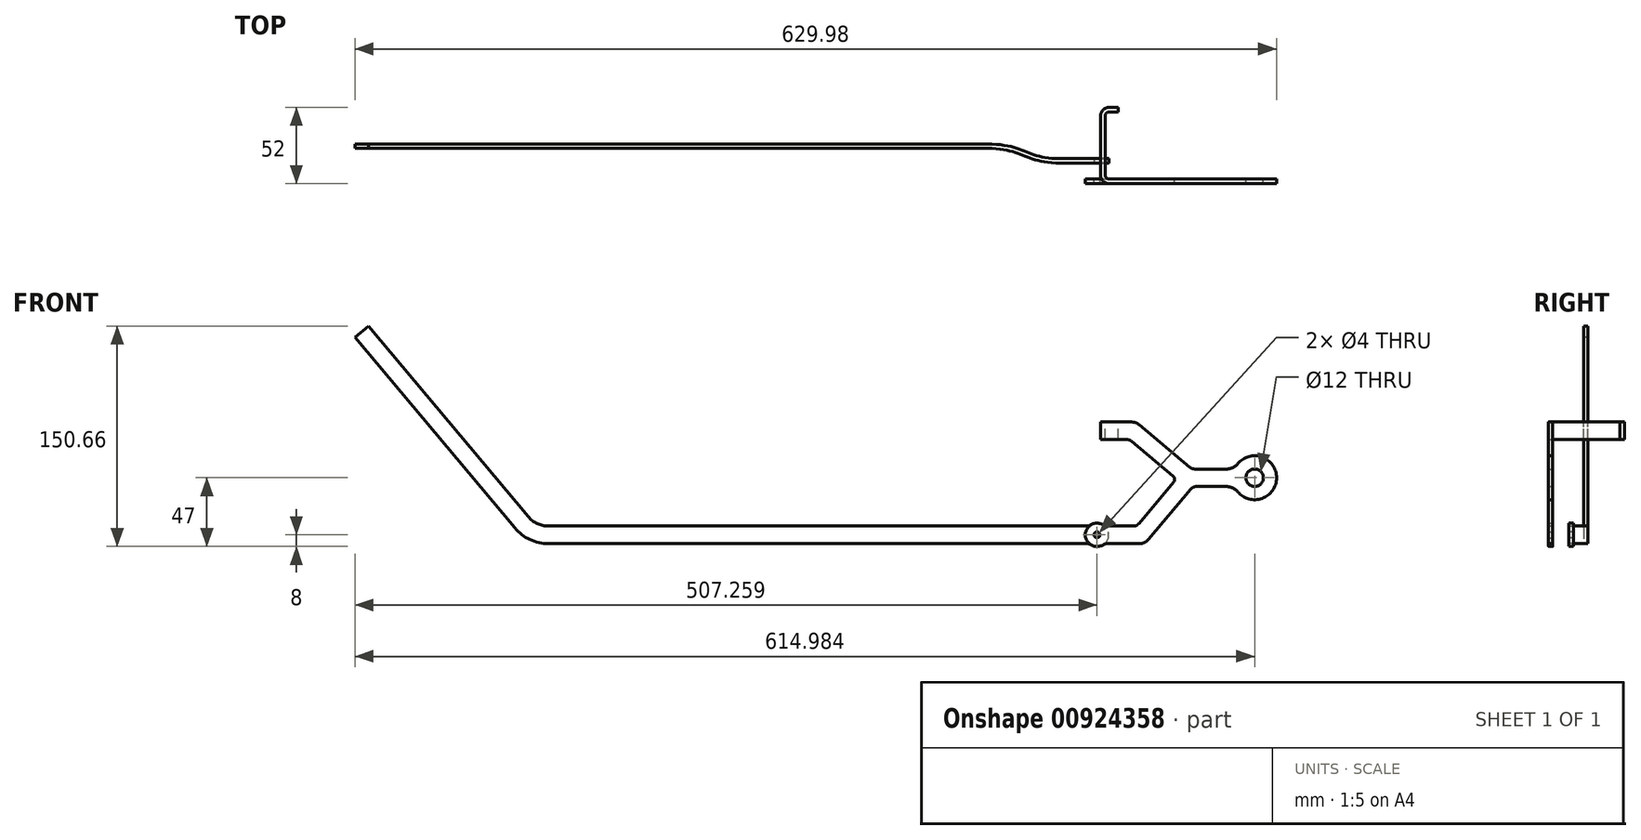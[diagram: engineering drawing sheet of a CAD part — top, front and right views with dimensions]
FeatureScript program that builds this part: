
annotation { "Feature Type Name" : "Feature", "Feature Type Description" : "" }
export const myFeature = defineFeature(function(context is Context, id is Id, definition is map)
    precondition{}
    {
        {
            var Q0;
            Q0=qCreatedBy(makeId("Front.planeOp"),FACE);
            var sketch = newSketch(context, id + "F0", { "sketchPlane" : qUnion([Q0])});
            skLineSegment(sketch, "E0", {"start": v(13.99, 0) * mm, "end": v(313.99, 0) * mm});
            skLineSegment(sketch, "E1", {"start": v(-9, 10.72) * mm, "end": v(-118.27, 140.94) * mm});
            skLineSegment(sketch, "E2", {"start": v(-23.81, 6) * mm, "end": v(-4.01, 6) * mm, "construction": true});
            skPoint(sketch, "E3.visualSharp", {"position": v(0, 0) * mm});
            skArc(sketch, "E3.filletArc", {"start": v(-9, 10.72) * mm, "mid": v(1.31, 2.81) * mm, "end": v(13.99, 0) * mm});
            skLineSegment(sketch, "E4.0", {"start": v(13.99, 12) * mm, "end": v(313.99, 12) * mm});
            skArc(sketch, "E4.1", {"start": v(0.2, 18.43) * mm, "mid": v(6.38, 13.69) * mm, "end": v(13.99, 12) * mm});
            skLineSegment(sketch, "E4.2", {"start": v(0.2, 18.43) * mm, "end": v(-109.07, 148.66) * mm});
            skLineSegment(sketch, "E5", {"start": v(-109.07, 148.66) * mm, "end": v(-118.27, 140.94) * mm});
            skLineSegment(sketch, "E6", {"start": v(313.99, 12) * mm, "end": v(313.99, 0) * mm});
            skSolve(sketch);
        }
        {
            var Q0;
            Q0=makeQuery(id+"F0.imprint","IMPRINT",FACE,{"disambiguationData":[TD([[makeQuery(id+"F0.imprint","IMPRINT",EDGE,{"derivedFrom":sQuery(id+"F0.wireOp",EDGE,"E0")}),1.0]])]});
            extrude(context, id + "F1", {"entities" : qUnion([Q0]), "depth" : 3 * mm, "offsetDistance" : 25 * mm});
        }
        {
            var Q0;
            Q0=qCreatedBy(makeId("Top.planeOp"),FACE);
            var sketch = newSketch(context, id + "F2", { "sketchPlane" : qUnion([Q0])});
            skLineSegment(sketch, "E7.0", {"start": v(13.99, 0) * mm, "end": v(313.99, 0) * mm});
            skSolve(sketch);
        }
        {
            var Q0;
            Q0=makeQuery(id+"F1.opExtrude","CAP_FACE",FACE,{"disambiguationData":[OSD([sQuery(id+"F0.wireOp",EDGE,"E0"),sQuery(id+"F0.wireOp",EDGE,"E1"),sQuery(id+"F0.wireOp",EDGE,"E3.filletArc"),sQuery(id+"F0.wireOp",EDGE,"E4.0"),sQuery(id+"F0.wireOp",EDGE,"E4.1"),sQuery(id+"F0.wireOp",EDGE,"E4.2"),sQuery(id+"F0.wireOp",EDGE,"E5"),sQuery(id+"F0.wireOp",EDGE,"E6")])],"isStart":true});
            cPlane(context, id + "F3", {"entities" : qUnion([Q0]), "cplaneType" : CPlaneType.OFFSET, "offset" : 25 * mm, "width" : 150 * mm, "height" : 150 * mm});
        }
        {
            var Q0;
            Q0=makeQuery(id+"F1.opExtrude","SWEPT_FACE",FACE,{"disambiguationData":[OSD([sQuery(id+"F0.wireOp",EDGE,"E0")])]});
            var sketch = newSketch(context, id + "F4", { "sketchPlane" : qUnion([Q0])});
            skPoint(sketch, "E8.0", {"position": v(313.99, 0) * mm});
            skFitSpline(sketch, "E9", {"points": [v(313.99, 0) * mm, v(363.99, -10) * mm], "startDerivative": vector(75, 0) * mm, "endDerivative": vector(75, 0) * mm});
            skLineSegment(sketch, "E10", {"start": v(363.99, -10) * mm, "end": v(388.99, -10) * mm});
            skLineSegment(sketch, "E11", {"start": v(363.99, -10) * mm, "end": v(241.15, -10) * mm, "construction": true});
            skSolve(sketch);
        }
        {
            var Q0;
            Q0=makeQuery(id+"F1.opExtrude","SWEPT_FACE",FACE,{"disambiguationData":[OSD([sQuery(id+"F0.wireOp",EDGE,"E6")])]});
            var Q1;
            Q1=sQuery(id+"F4.wireOp",EDGE,"E9");
            var Q2;
            Q2=sQuery(id+"F4.wireOp",EDGE,"E10");
            sweep(context, id + "F5", {"operationType" : NewBodyOperationType.ADD, "profiles" : qUnion([Q0]), "path" : qUnion([Q1, Q2])});
        }
        {
            var Q0;
            {var subQ0=sQuery(id+"F4.wireOp",EDGE,"E10");var subQ1=sQuery(id+"F0.wireOp",EDGE,"E6");Q0=makeQuery(id+"F5.opSweep","SWEPT_FACE",FACE,{"disambiguationData":[OSD([subQ1,subQ0]),TDD([makeQuery(id+"F1.opExtrude","CAP_EDGE",EDGE,{"disambiguationData":[OSD([subQ1])],"isStart":true}),subQ0])]});}
            var sketch = newSketch(context, id + "F6", { "sketchPlane" : qUnion([Q0])});
            skCircle(sketch, "E12", {"center": v(-388.99, 6) * mm, "radius": 6 * mm});
            skCircle(sketch, "E13", {"center": v(-388.99, 6) * mm, "radius": 2 * mm});
            skCircle(sketch, "E14", {"center": v(-388.99, 6) * mm, "radius": 8 * mm});
            skSolve(sketch);
        }
        {
            var Q0;
            {var subQ2=sQuery(id+"F0.wireOp",EDGE,"E6");var subQ4=sQuery(id+"F4.wireOp",EDGE,"E10");var subQ5=sQuery(id+"F0.wireOp",EDGE,"E0");var subQ6=makeQuery(id+"F5.opSweep","SWEPT_EDGE",EDGE,{"disambiguationData":[OSD([subQ5,subQ2,subQ4]),TDD([makeQuery(id+"F1.opExtrude","CAP_VERTEX",VERTEX,{"disambiguationData":[OSD([subQ5,subQ2])],"isStart":true}),subQ4])]});var subQ11=sQuery(id+"F6.wireOp",EDGE,"E14");var subQ13=makeQuery(id+"F6.imprint","INTERSECT",VERTEX,{"derivedFrom":[subQ6,subQ11]});Q0=makeQuery(id+"F6.imprint","IMPRINT",FACE,{"disambiguationData":[TD([[makeQuery(id+"F6.imprint","IMPRINT",EDGE,{"disambiguationData":[TD([[subQ13,1.0]])],"derivedFrom":subQ11}),1.0]])]});}
            var Q1;
            {var subQ1=sQuery(id+"F4.wireOp",VERTEX,"E10.end");var subQ2=sQuery(id+"F0.wireOp",EDGE,"E6");var subQ3=makeQuery(id+"F5.opSweep","CAP_EDGE",EDGE,{"disambiguationData":[OSD([subQ2,subQ1]),TDD([makeQuery(id+"F1.opExtrude","CAP_EDGE",EDGE,{"disambiguationData":[OSD([subQ2])],"isStart":true}),subQ1])],"isStart":false});var subQ9=sQuery(id+"F6.wireOp",EDGE,"E13");var subQ10=makeQuery(id+"F6.imprint","INTERSECT",VERTEX,{"disambiguationData":[OD(0.0)],"derivedFrom":[subQ3,subQ9]});Q1=makeQuery(id+"F6.imprint","IMPRINT",FACE,{"disambiguationData":[TD([[makeQuery(id+"F6.imprint","IMPRINT",EDGE,{"disambiguationData":[TD([[subQ10,1.0]])],"derivedFrom":subQ9}),-1.0]])]});}
            var Q2;
            {var subQ1=sQuery(id+"F4.wireOp",VERTEX,"E10.end");var subQ2=sQuery(id+"F0.wireOp",EDGE,"E6");var subQ3=makeQuery(id+"F5.opSweep","CAP_EDGE",EDGE,{"disambiguationData":[OSD([subQ2,subQ1]),TDD([makeQuery(id+"F1.opExtrude","CAP_EDGE",EDGE,{"disambiguationData":[OSD([subQ2])],"isStart":true}),subQ1])],"isStart":false});var subQ9=sQuery(id+"F6.wireOp",EDGE,"E13");var subQ10=makeQuery(id+"F6.imprint","INTERSECT",VERTEX,{"disambiguationData":[OD(0.0)],"derivedFrom":[subQ3,subQ9]});Q2=makeQuery(id+"F6.imprint","IMPRINT",FACE,{"disambiguationData":[TD([[makeQuery(id+"F6.imprint","IMPRINT",EDGE,{"disambiguationData":[TD([[subQ10,-1.0]])],"derivedFrom":subQ9}),-1.0]])]});}
            var Q3;
            {var subQ2=sQuery(id+"F0.wireOp",EDGE,"E6");var subQ4=sQuery(id+"F4.wireOp",EDGE,"E10");var subQ5=sQuery(id+"F0.wireOp",EDGE,"E0");var subQ6=makeQuery(id+"F5.opSweep","SWEPT_EDGE",EDGE,{"disambiguationData":[OSD([subQ5,subQ2,subQ4]),TDD([makeQuery(id+"F1.opExtrude","CAP_VERTEX",VERTEX,{"disambiguationData":[OSD([subQ5,subQ2])],"isStart":true}),subQ4])]});var subQ11=sQuery(id+"F6.wireOp",EDGE,"E14");var subQ12=makeQuery(id+"F6.imprint","INTERSECT",VERTEX,{"derivedFrom":[subQ6,subQ11]});Q3=makeQuery(id+"F6.imprint","IMPRINT",FACE,{"disambiguationData":[TD([[makeQuery(id+"F6.imprint","IMPRINT",EDGE,{"disambiguationData":[TD([[subQ12,-1.0]])],"derivedFrom":subQ11}),1.0]])]});}
            var Q4;
            {var subQ0=sQuery(id+"F6.wireOp",EDGE,"E13");var subQ1=sQuery(id+"F4.wireOp",VERTEX,"E10.end");var subQ2=sQuery(id+"F0.wireOp",EDGE,"E6");var subQ3=makeQuery(id+"F5.opSweep","CAP_EDGE",EDGE,{"disambiguationData":[OSD([subQ2,subQ1]),TDD([makeQuery(id+"F1.opExtrude","CAP_EDGE",EDGE,{"disambiguationData":[OSD([subQ2])],"isStart":true}),subQ1])],"isStart":false});var subQ4=makeQuery(id+"F6.imprint","INTERSECT",VERTEX,{"disambiguationData":[OD(0.0)],"derivedFrom":[subQ3,subQ0]});Q4=makeQuery(id+"F6.imprint","IMPRINT",FACE,{"disambiguationData":[TD([[makeQuery(id+"F6.imprint","IMPRINT",EDGE,{"disambiguationData":[TD([[subQ4,1.0]])],"derivedFrom":subQ0}),1.0]])]});}
            var Q5;
            {var subQ0=sQuery(id+"F6.wireOp",EDGE,"E13");var subQ1=sQuery(id+"F4.wireOp",VERTEX,"E10.end");var subQ2=sQuery(id+"F0.wireOp",EDGE,"E6");var subQ3=makeQuery(id+"F5.opSweep","CAP_EDGE",EDGE,{"disambiguationData":[OSD([subQ2,subQ1]),TDD([makeQuery(id+"F1.opExtrude","CAP_EDGE",EDGE,{"disambiguationData":[OSD([subQ2])],"isStart":true}),subQ1])],"isStart":false});var subQ4=makeQuery(id+"F6.imprint","INTERSECT",VERTEX,{"disambiguationData":[OD(0.0)],"derivedFrom":[subQ3,subQ0]});Q5=makeQuery(id+"F6.imprint","IMPRINT",FACE,{"disambiguationData":[TD([[makeQuery(id+"F6.imprint","IMPRINT",EDGE,{"disambiguationData":[TD([[subQ4,-1.0]])],"derivedFrom":subQ0}),1.0]])]});}
            extrude(context, id + "F7", {"entities" : qUnion([Q0, Q1, Q2, Q3, Q4, Q5]), "operationType" : NewBodyOperationType.ADD, "oppositeDirection" : true, "depth" : 3 * mm, "offsetDistance" : 25 * mm});
        }
        {
            var Q0;
            {var subQ0=sQuery(id+"F6.wireOp",EDGE,"E13");var subQ1=sQuery(id+"F4.wireOp",VERTEX,"E10.end");var subQ2=sQuery(id+"F0.wireOp",EDGE,"E6");var subQ3=makeQuery(id+"F5.opSweep","CAP_EDGE",EDGE,{"disambiguationData":[OSD([subQ2,subQ1]),TDD([makeQuery(id+"F1.opExtrude","CAP_EDGE",EDGE,{"disambiguationData":[OSD([subQ2])],"isStart":true}),subQ1])],"isStart":false});var subQ4=makeQuery(id+"F6.imprint","INTERSECT",VERTEX,{"disambiguationData":[OD(0.0)],"derivedFrom":[subQ3,subQ0]});Q0=makeQuery(id+"F6.imprint","IMPRINT",FACE,{"disambiguationData":[TD([[makeQuery(id+"F6.imprint","IMPRINT",EDGE,{"disambiguationData":[TD([[subQ4,1.0]])],"derivedFrom":subQ0}),1.0]])]});}
            var Q1;
            {var subQ0=sQuery(id+"F6.wireOp",EDGE,"E13");var subQ1=sQuery(id+"F4.wireOp",VERTEX,"E10.end");var subQ2=sQuery(id+"F0.wireOp",EDGE,"E6");var subQ3=makeQuery(id+"F5.opSweep","CAP_EDGE",EDGE,{"disambiguationData":[OSD([subQ2,subQ1]),TDD([makeQuery(id+"F1.opExtrude","CAP_EDGE",EDGE,{"disambiguationData":[OSD([subQ2])],"isStart":true}),subQ1])],"isStart":false});var subQ4=makeQuery(id+"F6.imprint","INTERSECT",VERTEX,{"disambiguationData":[OD(0.0)],"derivedFrom":[subQ3,subQ0]});Q1=makeQuery(id+"F6.imprint","IMPRINT",FACE,{"disambiguationData":[TD([[makeQuery(id+"F6.imprint","IMPRINT",EDGE,{"disambiguationData":[TD([[subQ4,-1.0]])],"derivedFrom":subQ0}),1.0]])]});}
            extrude(context, id + "F8", {"entities" : qUnion([Q0, Q1]), "operationType" : NewBodyOperationType.REMOVE, "oppositeDirection" : true, "depth" : 25 * mm, "offsetDistance" : 25 * mm});
        }
        {
            var Q0;
            {var subQ0=sQuery(id+"F0.wireOp",EDGE,"E4.0");Q0=makeQuery(id+"F7.boolean.opBoolean","INTERSECT",EDGE,{"derivedFrom":[makeQuery(id+"F5.boolean.opBoolean","MERGE",FACE,{"derivedFrom":[makeQuery(id+"F1.opExtrude","SWEPT_FACE",FACE,{"disambiguationData":[OSD([subQ0])]}),makeQuery(id+"F5.opSweep","SWEPT_FACE",FACE,{"disambiguationData":[OSD([subQ0,sQuery(id+"F0.wireOp",EDGE,"E6"),sQuery(id+"F4.wireOp",EDGE,"E9")])]})]}),makeQuery(id+"F7.opExtrude","SWEPT_FACE",FACE,{"disambiguationData":[OSD([sQuery(id+"F6.wireOp",EDGE,"E14")])]})]});}
            var Q1;
            {var subQ0=sQuery(id+"F0.wireOp",EDGE,"E0");Q1=makeQuery(id+"F7.boolean.opBoolean","INTERSECT",EDGE,{"derivedFrom":[makeQuery(id+"F5.boolean.opBoolean","MERGE",FACE,{"derivedFrom":[makeQuery(id+"F1.opExtrude","SWEPT_FACE",FACE,{"disambiguationData":[OSD([subQ0])]}),makeQuery(id+"F5.opSweep","SWEPT_FACE",FACE,{"disambiguationData":[OSD([subQ0,sQuery(id+"F0.wireOp",EDGE,"E6"),sQuery(id+"F4.wireOp",EDGE,"E9")])]})]}),makeQuery(id+"F7.opExtrude","SWEPT_FACE",FACE,{"disambiguationData":[OSD([sQuery(id+"F6.wireOp",EDGE,"E14")])]})]});}
            fillet(context, id + "F9", {"entities" : qUnion([Q0, Q1]), "radius" : 5 * mm, "tangentPropagation" : true, "allowEdgeOverflow" : false});
        }
        {
            var Q0;
            Q0=qCreatedBy(id+"F3.planeOp",FACE);
            var sketch = newSketch(context, id + "F10", { "sketchPlane" : qUnion([Q0])});
            skArc(sketch, "E15.0", {"start": v(-393.25, -0.77) * mm, "mid": v(-380.99, 6) * mm, "end": v(-393.25, 12.77) * mm});
            skPoint(sketch, "E16.orphan", {"position": v(-382.06, 12) * mm});
            skPoint(sketch, "E17.orphan", {"position": v(-388.99, 0) * mm});
            skPoint(sketch, "E18.orphan", {"position": v(-363.99, 12) * mm});
            skPoint(sketch, "E19.orphan", {"position": v(-363.99, 0) * mm});
            skLineSegment(sketch, "E20", {"start": v(-363.99, 0) * mm, "end": v(-363.99, -55) * mm, "construction": true});
            skLineSegment(sketch, "E21", {"start": v(-363.99, -55) * mm, "end": v(-590.7, -55) * mm, "construction": true});
            skCircle(sketch, "E22", {"center": v(-496.71, 45) * mm, "radius": 100 * mm});
            skArc(sketch, "E23", {"start": v(-485.19, 54.6) * mm, "mid": v(-511.71, 45) * mm, "end": v(-485.19, 35.4) * mm});
            skLineSegment(sketch, "E24", {"start": v(-388.99, 6) * mm, "end": v(-418.99, 6) * mm, "construction": true});
            skLineSegment(sketch, "E25", {"start": v(-418.99, 6) * mm, "end": v(-451.71, 45) * mm, "construction": true});
            skLineSegment(sketch, "E26", {"start": v(-451.71, 45) * mm, "end": v(-481.71, 45) * mm, "construction": true});
            skLineSegment(sketch, "E27.0", {"start": v(-455.72, 51) * mm, "end": v(-477.5, 51) * mm});
            skLineSegment(sketch, "E27.1", {"start": v(-417.7, 13.79) * mm, "end": v(-441.33, 41.96) * mm});
            skLineSegment(sketch, "E27.2", {"start": v(-395.92, 12) * mm, "end": v(-413.86, 12) * mm});
            skLineSegment(sketch, "E28.0", {"start": v(-456.84, 39) * mm, "end": v(-477.5, 39) * mm});
            skLineSegment(sketch, "E28.1", {"start": v(-424.18, 2.86) * mm, "end": v(-453.01, 37.21) * mm});
            skLineSegment(sketch, "E28.2", {"start": v(-395.92, 0) * mm, "end": v(-418.06, 0) * mm});
            skPoint(sketch, "E29.visualSharp", {"position": v(-482.97, 51) * mm});
            skArc(sketch, "E29.filletArc", {"start": v(-485.19, 54.6) * mm, "mid": v(-481.75, 51.94) * mm, "end": v(-477.5, 51) * mm});
            skPoint(sketch, "E30.visualSharp", {"position": v(-482.97, 39) * mm});
            skArc(sketch, "E30.filletArc", {"start": v(-477.5, 39) * mm, "mid": v(-481.75, 38.06) * mm, "end": v(-485.19, 35.4) * mm});
            skPoint(sketch, "E31.visualSharp", {"position": v(-454.51, 39) * mm});
            skArc(sketch, "E31.filletArc", {"start": v(-453.01, 37.21) * mm, "mid": v(-454.73, 38.53) * mm, "end": v(-456.84, 39) * mm});
            skPoint(sketch, "E32.visualSharp", {"position": v(-448.92, 51) * mm});
            skPoint(sketch, "E33.visualSharp", {"position": v(-416.2, 12) * mm});
            skArc(sketch, "E33.filletArc", {"start": v(-417.7, 13.79) * mm, "mid": v(-415.97, 12.47) * mm, "end": v(-413.86, 12) * mm});
            skPoint(sketch, "E34.visualSharp", {"position": v(-421.79, 0) * mm});
            skArc(sketch, "E34.filletArc", {"start": v(-424.18, 2.86) * mm, "mid": v(-421.44, 0.75) * mm, "end": v(-418.06, 0) * mm});
            skPoint(sketch, "E35.visualSharp", {"position": v(-394.28, 12) * mm});
            skArc(sketch, "E35.filletArc", {"start": v(-395.92, 12) * mm, "mid": v(-394.53, 12.2) * mm, "end": v(-393.25, 12.77) * mm});
            skPoint(sketch, "E36.visualSharp", {"position": v(-394.28, 0) * mm});
            skArc(sketch, "E36.filletArc", {"start": v(-393.25, -0.77) * mm, "mid": v(-394.53, -0.2) * mm, "end": v(-395.92, 0) * mm});
            skCircle(sketch, "E37", {"center": v(-496.71, 45) * mm, "radius": 6 * mm});
            skCircle(sketch, "E38.0", {"center": v(-388.99, 6) * mm, "radius": 2 * mm});
            skLineSegment(sketch, "E39", {"start": v(-451.71, 45) * mm, "end": v(-413.45, 77.1) * mm, "construction": true});
            skLineSegment(sketch, "E40.0", {"start": v(-452.5, 52.17) * mm, "end": v(-417.87, 81.23) * mm});
            skLineSegment(sketch, "E41.0", {"start": v(-440.96, 46.19) * mm, "end": v(-412.66, 69.94) * mm});
            skPoint(sketch, "E42.visualSharp", {"position": v(-453.9, 51) * mm});
            skArc(sketch, "E42.filletArc", {"start": v(-455.72, 51) * mm, "mid": v(-454, 51.3) * mm, "end": v(-452.5, 52.17) * mm});
            skPoint(sketch, "E43.visualSharp", {"position": v(-443.26, 44.26) * mm});
            skArc(sketch, "E43.filletArc", {"start": v(-440.96, 46.19) * mm, "mid": v(-442.02, 44.15) * mm, "end": v(-441.33, 41.96) * mm});
            skLineSegment(sketch, "E44", {"start": v(-413.45, 77.1) * mm, "end": v(-403.45, 77.1) * mm, "construction": true});
            skLineSegment(sketch, "E45.0", {"start": v(-409.45, 71.1) * mm, "end": v(-403.45, 71.1) * mm});
            skLineSegment(sketch, "E46.0", {"start": v(-412.72, 83.1) * mm, "end": v(-403.45, 83.1) * mm});
            skLineSegment(sketch, "E47", {"start": v(-403.45, 71.1) * mm, "end": v(-403.45, 83.1) * mm});
            skPoint(sketch, "E48.visualSharp", {"position": v(-415.64, 83.1) * mm});
            skArc(sketch, "E48.filletArc", {"start": v(-412.72, 83.1) * mm, "mid": v(-415.46, 82.62) * mm, "end": v(-417.87, 81.23) * mm});
            skPoint(sketch, "E49.visualSharp", {"position": v(-411.27, 71.1) * mm});
            skArc(sketch, "E49.filletArc", {"start": v(-409.45, 71.1) * mm, "mid": v(-411.16, 70.8) * mm, "end": v(-412.66, 69.94) * mm});
            skSolve(sketch);
        }
        {
            var Q0;
            Q0=makeQuery(id+"F10.imprint","IMPRINT",FACE,{"disambiguationData":[TD([[makeQuery(id+"F10.imprint","IMPRINT",EDGE,{"derivedFrom":sQuery(id+"F10.wireOp",EDGE,"E23")}),1.0]])]});
            var Q1;
            Q1=makeQuery(id+"F10.imprint","IMPRINT",FACE,{"disambiguationData":[TD([[makeQuery(id+"F10.imprint","IMPRINT",EDGE,{"derivedFrom":sQuery(id+"F10.wireOp",EDGE,"E15.0")}),1.0]])]});
            var Q2;
            {var subQ5=sQuery(id+"F10.wireOp",EDGE,"E47");Q2=makeQuery(id+"F10.imprint","IMPRINT",FACE,{"disambiguationData":[TD([[makeQuery(id+"F10.imprint","IMPRINT",EDGE,{"derivedFrom":subQ5}),1.0]])]});}
            extrude(context, id + "F11", {"entities" : qUnion([Q0, Q1, Q2]), "depth" : 3 * mm, "offsetDistance" : 25 * mm});
        }
        {
            var Q0;
            Q0=makeQuery(id+"F11.opExtrude","SWEPT_FACE",FACE,{"disambiguationData":[OSD([sQuery(id+"F10.wireOp",EDGE,"E46.0")])]});
            var sketch = newSketch(context, id + "F12", { "sketchPlane" : qUnion([Q0])});
            skLineSegment(sketch, "E50.0", {"start": v(412.72, 25) * mm, "end": v(403.45, 25) * mm});
            skLineSegment(sketch, "E51", {"start": v(403.45, 25) * mm, "end": v(397.45, 25) * mm});
            skLineSegment(sketch, "E52", {"start": v(394.45, 22) * mm, "end": v(394.45, -18) * mm});
            skPoint(sketch, "E53.visualSharp", {"position": v(394.45, 25) * mm});
            skArc(sketch, "E53.filletArc", {"start": v(397.45, 25) * mm, "mid": v(395.33, 24.12) * mm, "end": v(394.45, 22) * mm});
            skLineSegment(sketch, "E54", {"start": v(394.45, 2) * mm, "end": v(428.98, 2) * mm, "construction": true});
            skLineSegment(sketch, "E55.MirrorCS", {"start": v(403.45, -21) * mm, "end": v(397.45, -21) * mm});
            skArc(sketch, "E56.MirrorCS", {"start": v(397.45, -21) * mm, "mid": v(395.33, -20.12) * mm, "end": v(394.45, -18) * mm});
            skSolve(sketch);
        }
        {
            var Q0;
            Q0=makeQuery(id+"F11.opExtrude","SWEPT_FACE",FACE,{"disambiguationData":[OSD([sQuery(id+"F10.wireOp",EDGE,"E47")])]});
            var sketch = newSketch(context, id + "F13", { "sketchPlane" : qUnion([Q0])});
            skLineSegment(sketch, "E57.0.0", {"start": v(-25, 71.1) * mm, "end": v(-25, 83.1) * mm});
            skLineSegment(sketch, "E57.0.1", {"start": v(-25, 83.1) * mm, "end": v(-28, 83.1) * mm});
            skLineSegment(sketch, "E57.0.2", {"start": v(-28, 83.1) * mm, "end": v(-28, 71.1) * mm});
            skLineSegment(sketch, "E57.0.3", {"start": v(-28, 71.1) * mm, "end": v(-25, 71.1) * mm});
            skSolve(sketch);
        }
        {
            var Q0;
            Q0=makeQuery(id+"F13.imprint","IMPRINT",FACE,{"disambiguationData":[TD([[makeQuery(id+"F13.imprint","IMPRINT",EDGE,{"derivedFrom":sQuery(id+"F13.wireOp",EDGE,"E57.0.0")}),1.0]])]});
            var Q1;
            Q1=sQuery(id+"F12.wireOp",EDGE,"E51");
            var Q2;
            Q2=sQuery(id+"F12.wireOp",EDGE,"E53.filletArc");
            var Q3;
            Q3=sQuery(id+"F12.wireOp",EDGE,"E52");
            var Q4;
            Q4=sQuery(id+"F12.wireOp",EDGE,"E56.MirrorCS");
            var Q5;
            Q5=sQuery(id+"F12.wireOp",EDGE,"E55.MirrorCS");
            sweep(context, id + "F14", {"operationType" : NewBodyOperationType.ADD, "profiles" : qUnion([Q0]), "path" : qUnion([Q1, Q2, Q3, Q4, Q5])});
        }
        {
            var Q0;
            Q0=sQuery(id+"F12.wireOp",EDGE,"E54");
            cPlane(context, id + "F15", {"entities" : qUnion([Q0]), "cplaneType" : CPlaneType.LINE_ANGLE, "offset" : 25 * mm, "angle" : 0 * degree, "width" : 150 * mm, "height" : 150 * mm});
        }
        {
            var Q0;
            Q0=makeQuery(id+"F11.opExtrude","SWEPT_BODY",BODY,{"disambiguationData":[OSD([sQuery(id+"F10.wireOp",EDGE,"E15.0"),sQuery(id+"F10.wireOp",EDGE,"E23"),sQuery(id+"F10.wireOp",EDGE,"E27.0"),sQuery(id+"F10.wireOp",EDGE,"E27.1"),sQuery(id+"F10.wireOp",EDGE,"E27.2"),sQuery(id+"F10.wireOp",EDGE,"E28.0"),sQuery(id+"F10.wireOp",EDGE,"E28.1"),sQuery(id+"F10.wireOp",EDGE,"E28.2"),sQuery(id+"F10.wireOp",EDGE,"E29.filletArc"),sQuery(id+"F10.wireOp",EDGE,"E30.filletArc"),sQuery(id+"F10.wireOp",EDGE,"E31.filletArc"),sQuery(id+"F10.wireOp",EDGE,"E33.filletArc"),sQuery(id+"F10.wireOp",EDGE,"E34.filletArc"),sQuery(id+"F10.wireOp",EDGE,"E35.filletArc"),sQuery(id+"F10.wireOp",EDGE,"E36.filletArc"),sQuery(id+"F10.wireOp",EDGE,"E37"),sQuery(id+"F10.wireOp",EDGE,"E38.0"),sQuery(id+"F10.wireOp",EDGE,"E40.0"),sQuery(id+"F10.wireOp",EDGE,"E41.0"),sQuery(id+"F10.wireOp",EDGE,"E42.filletArc"),sQuery(id+"F10.wireOp",EDGE,"E43.filletArc"),sQuery(id+"F10.wireOp",EDGE,"E45.0"),sQuery(id+"F10.wireOp",EDGE,"E46.0"),sQuery(id+"F10.wireOp",EDGE,"E47"),sQuery(id+"F10.wireOp",EDGE,"E48.filletArc"),sQuery(id+"F10.wireOp",EDGE,"E49.filletArc")])]});
            var Q1;
            Q1=qCreatedBy(id+"F15.planeOp",FACE);
            mirror(context, id + "F16", {"operationType" : NewBodyOperationType.ADD, "entities" : qUnion([Q0]), "mirrorPlane" : qUnion([Q1])});
        }
        {
            var Q0;
            Q0=makeQuery(id+"F11.opExtrude","SWEPT_BODY",BODY,{"disambiguationData":[OSD([sQuery(id+"F10.wireOp",EDGE,"E15.0"),sQuery(id+"F10.wireOp",EDGE,"E23"),sQuery(id+"F10.wireOp",EDGE,"E27.0"),sQuery(id+"F10.wireOp",EDGE,"E27.1"),sQuery(id+"F10.wireOp",EDGE,"E27.2"),sQuery(id+"F10.wireOp",EDGE,"E28.0"),sQuery(id+"F10.wireOp",EDGE,"E28.1"),sQuery(id+"F10.wireOp",EDGE,"E28.2"),sQuery(id+"F10.wireOp",EDGE,"E29.filletArc"),sQuery(id+"F10.wireOp",EDGE,"E30.filletArc"),sQuery(id+"F10.wireOp",EDGE,"E31.filletArc"),sQuery(id+"F10.wireOp",EDGE,"E33.filletArc"),sQuery(id+"F10.wireOp",EDGE,"E34.filletArc"),sQuery(id+"F10.wireOp",EDGE,"E35.filletArc"),sQuery(id+"F10.wireOp",EDGE,"E36.filletArc"),sQuery(id+"F10.wireOp",EDGE,"E37"),sQuery(id+"F10.wireOp",EDGE,"E38.0"),sQuery(id+"F10.wireOp",EDGE,"E40.0"),sQuery(id+"F10.wireOp",EDGE,"E41.0"),sQuery(id+"F10.wireOp",EDGE,"E42.filletArc"),sQuery(id+"F10.wireOp",EDGE,"E43.filletArc"),sQuery(id+"F10.wireOp",EDGE,"E45.0"),sQuery(id+"F10.wireOp",EDGE,"E46.0"),sQuery(id+"F10.wireOp",EDGE,"E47"),sQuery(id+"F10.wireOp",EDGE,"E48.filletArc"),sQuery(id+"F10.wireOp",EDGE,"E49.filletArc")])]});
            deleteBodies(context, id + "F17", {"entities" : qUnion([Q0])});
        }
        {
            var Q0;
            Q0=makeQuery(id+"F1.opExtrude","SWEPT_BODY",BODY,{"disambiguationData":[OSD([sQuery(id+"F0.wireOp",EDGE,"E0"),sQuery(id+"F0.wireOp",EDGE,"E1"),sQuery(id+"F0.wireOp",EDGE,"E3.filletArc"),sQuery(id+"F0.wireOp",EDGE,"E4.0"),sQuery(id+"F0.wireOp",EDGE,"E4.1"),sQuery(id+"F0.wireOp",EDGE,"E4.2"),sQuery(id+"F0.wireOp",EDGE,"E5"),sQuery(id+"F0.wireOp",EDGE,"E6")])]});
            var Q1;
            Q1=qCreatedBy(makeId("Front.planeOp"),FACE);
            mirror(context, id + "F18", {"entities" : qUnion([Q0]), "mirrorPlane" : qUnion([Q1])});
        }
        {
            var Q0;
            Q0=makeQuery(id+"F1.opExtrude","SWEPT_BODY",BODY,{"disambiguationData":[OSD([sQuery(id+"F0.wireOp",EDGE,"E0"),sQuery(id+"F0.wireOp",EDGE,"E1"),sQuery(id+"F0.wireOp",EDGE,"E3.filletArc"),sQuery(id+"F0.wireOp",EDGE,"E4.0"),sQuery(id+"F0.wireOp",EDGE,"E4.1"),sQuery(id+"F0.wireOp",EDGE,"E4.2"),sQuery(id+"F0.wireOp",EDGE,"E5"),sQuery(id+"F0.wireOp",EDGE,"E6")])]});
            deleteBodies(context, id + "F19", {"entities" : qUnion([Q0])});
        }
    });
